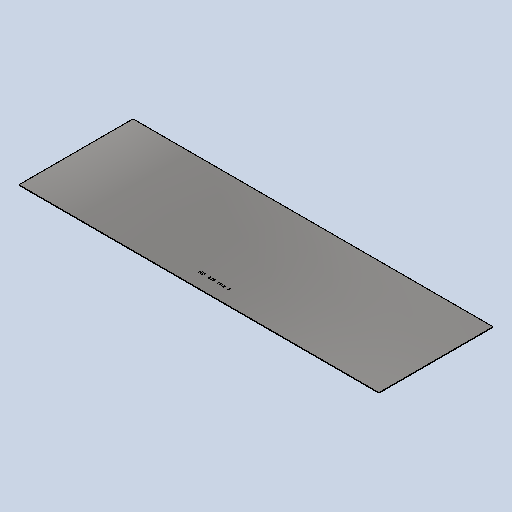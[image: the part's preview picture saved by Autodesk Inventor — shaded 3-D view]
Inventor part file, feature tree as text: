
AUTODESK INVENTOR PART (.ipt)
format: ipt  version: 2025 (Build 290162010, 162A)  size: 290,304 bytes
history: native  units: mm
features: other x2, sketch x2, sheet_metal_op x1
ambient origin geometry x8: Origin, YZ Plane, XZ Plane, XY Plane, X Axis, Y Axis, Z Axis, Center Point
bodies: Solid1 (feature_tree)
feature tree (5):
  sheet_metal_op  "Face1"
  other  "Mark1"
  sketch  "Sketch1"  dims[d0=1344.0mm]
  other  "Plate1"
  sketch  "Sketch2"  dims[d1=426.0mm d2=2.0mm d3=12.0mm d4=110.0mm d5=50.0mm]
